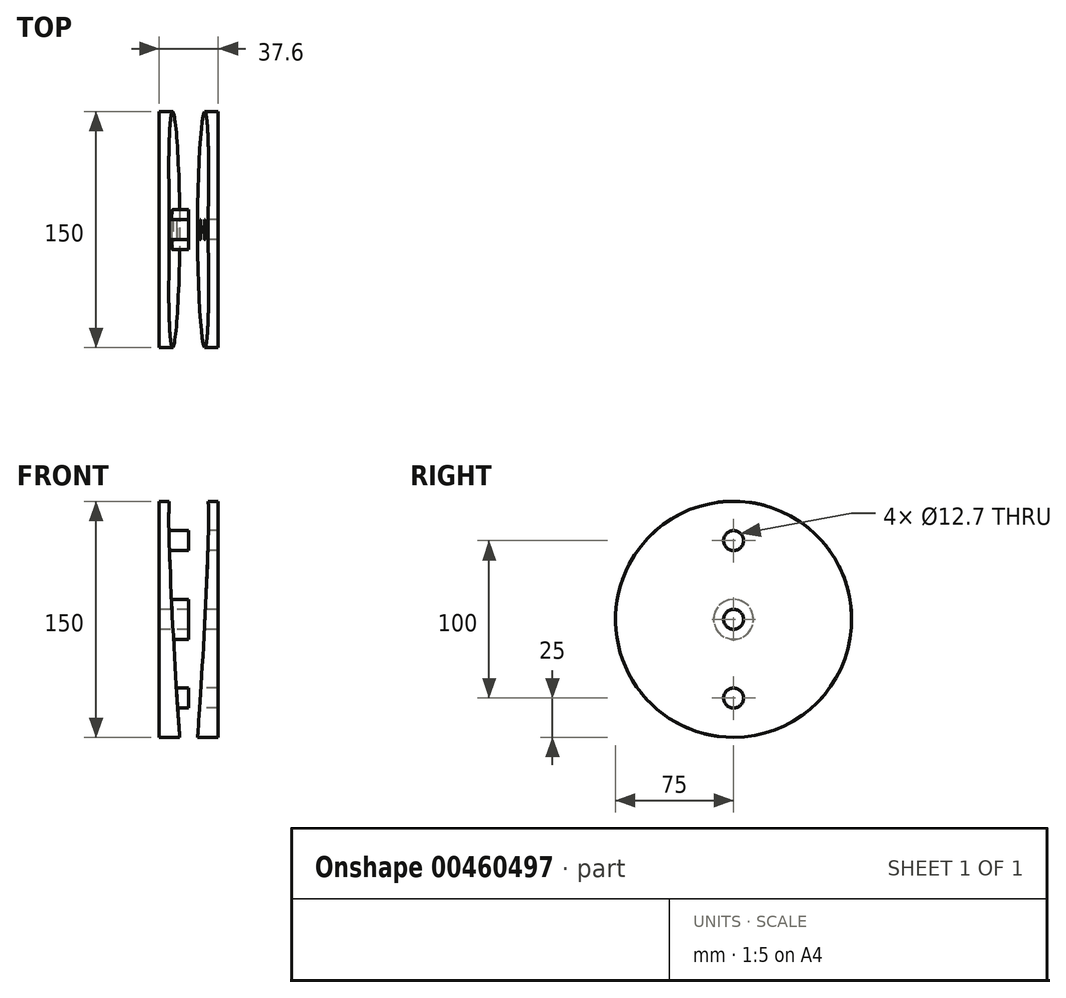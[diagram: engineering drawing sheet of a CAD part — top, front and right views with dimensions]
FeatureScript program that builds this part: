
annotation { "Feature Type Name" : "Feature", "Feature Type Description" : "" }
export const myFeature = defineFeature(function(context is Context, id is Id, definition is map)
    precondition{}
    {
        {
            var Q0;
            Q0=qCreatedBy(makeId("Front.planeOp"),FACE);
            var sketch = newSketch(context, id + "F0", { "sketchPlane" : qUnion([Q0])});
            skLineSegment(sketch, "E0", {"start": v(-26, 84.74) * mm, "end": v(-24.5, 84.74) * mm});
            skArc(sketch, "E1", {"start": v(-26.25, 85) * mm, "mid": v(-26.17, 84.82) * mm, "end": v(-26, 84.74) * mm});
            skFitSpline(sketch, "E2", {"points": [v(-26.25, 85) * mm, v(-26.24, 88.67) * mm, v(-26.08, 98.58) * mm, v(-25.1, 113) * mm, v(-22.87, 125.21) * mm, v(-20.9, 130.42) * mm, v(-19.33, 133.17) * mm, v(-17.9, 134.65) * mm, v(-16.79, 135) * mm, v(-16.24, 135) * mm]});
            skFitSpline(sketch, "E3", {"points": [v(-16.24, 135) * mm, v(-15.7, 135) * mm, v(-14.58, 134.65) * mm, v(-13.16, 133.17) * mm, v(-11.58, 130.42) * mm, v(-9.61, 125.21) * mm, v(-7.38, 113) * mm, v(-6.4, 98.58) * mm, v(-6.24, 88.67) * mm, v(-6.24, 85) * mm]});
            skArc(sketch, "E4", {"start": v(-6.49, 84.74) * mm, "mid": v(-6.3, 84.82) * mm, "end": v(-6.24, 85) * mm});
            skLineSegment(sketch, "E5", {"start": v(-7.99, 84.74) * mm, "end": v(-6.49, 84.74) * mm});
            skArc(sketch, "E6", {"start": v(-7.99, 84.74) * mm, "mid": v(-8.16, 84.67) * mm, "end": v(-8.24, 84.5) * mm});
            skLineSegment(sketch, "E7", {"start": v(-8.24, 84.5) * mm, "end": v(-8.24, 75) * mm});
            skArc(sketch, "E8", {"start": v(-10.24, 88.79) * mm, "mid": v(-10.27, 88.98) * mm, "end": v(-10.38, 89.14) * mm});
            skLineSegment(sketch, "E9", {"start": v(-11.41, 90.17) * mm, "end": v(-10.38, 89.14) * mm});
            skArc(sketch, "E10", {"start": v(-11.44, 90.85) * mm, "mid": v(-11.56, 90.5) * mm, "end": v(-11.41, 90.17) * mm});
            skArc(sketch, "E11", {"start": v(-11.44, 90.85) * mm, "mid": v(-9.9, 95) * mm, "end": v(-11.44, 99.15) * mm});
            skArc(sketch, "E12", {"start": v(-11.41, 99.83) * mm, "mid": v(-11.56, 99.5) * mm, "end": v(-11.44, 99.15) * mm});
            skLineSegment(sketch, "E13", {"start": v(-11.41, 99.83) * mm, "end": v(-9.68, 101.56) * mm});
            skArc(sketch, "E14", {"start": v(-9.68, 101.56) * mm, "mid": v(-9, 102.63) * mm, "end": v(-8.81, 103.89) * mm});
            skFitSpline(sketch, "E15", {"points": [v(-8.81, 103.89) * mm, v(-8.97, 106.15) * mm, v(-9.72, 114.71) * mm, v(-11.32, 123.38) * mm, v(-12.63, 127.4) * mm, v(-12.98, 128.32) * mm]});
            skArc(sketch, "E16", {"start": v(-12.98, 128.32) * mm, "mid": v(-13.34, 128.63) * mm, "end": v(-13.8, 128.5) * mm});
            skArc(sketch, "E17", {"start": v(-14.5, 127.97) * mm, "mid": v(-14.13, 128.21) * mm, "end": v(-13.8, 128.5) * mm});
            skArc(sketch, "E18", {"start": v(-15.24, 128.4) * mm, "mid": v(-15, 127.97) * mm, "end": v(-14.5, 127.97) * mm});
            skLineSegment(sketch, "E19", {"start": v(-15.24, 129) * mm, "end": v(-15.24, 128.4) * mm});
            skArc(sketch, "E20", {"start": v(-15.04, 129.4) * mm, "mid": v(-15.19, 129.22) * mm, "end": v(-15.24, 129) * mm});
            skArc(sketch, "E21", {"start": v(-15.04, 129.4) * mm, "mid": v(-16.24, 133) * mm, "end": v(-17.44, 129.4) * mm});
            skArc(sketch, "E22", {"start": v(-17.24, 129) * mm, "mid": v(-17.3, 129.22) * mm, "end": v(-17.44, 129.4) * mm});
            skLineSegment(sketch, "E23", {"start": v(-17.24, 128.4) * mm, "end": v(-17.24, 129) * mm});
            skArc(sketch, "E24", {"start": v(-18, 127.97) * mm, "mid": v(-17.5, 127.97) * mm, "end": v(-17.24, 128.4) * mm});
            skArc(sketch, "E25", {"start": v(-18.69, 128.5) * mm, "mid": v(-18.36, 128.21) * mm, "end": v(-18, 127.97) * mm});
            skArc(sketch, "E26", {"start": v(-18.69, 128.5) * mm, "mid": v(-19.15, 128.63) * mm, "end": v(-19.5, 128.32) * mm});
            skFitSpline(sketch, "E27", {"points": [v(-19.5, 128.32) * mm, v(-19.86, 127.4) * mm, v(-21.16, 123.38) * mm, v(-22.76, 114.71) * mm, v(-23.52, 106.15) * mm, v(-23.67, 103.89) * mm]});
            skArc(sketch, "E28", {"start": v(-23.67, 103.89) * mm, "mid": v(-23.49, 102.63) * mm, "end": v(-22.8, 101.56) * mm});
            skLineSegment(sketch, "E29", {"start": v(-22.8, 101.56) * mm, "end": v(-21.07, 99.83) * mm});
            skArc(sketch, "E30", {"start": v(-21.05, 99.15) * mm, "mid": v(-20.93, 99.5) * mm, "end": v(-21.07, 99.83) * mm});
            skArc(sketch, "E31", {"start": v(-21.05, 99.15) * mm, "mid": v(-22.6, 95) * mm, "end": v(-21.05, 90.85) * mm});
            skArc(sketch, "E32", {"start": v(-21.07, 90.17) * mm, "mid": v(-20.93, 90.5) * mm, "end": v(-21.05, 90.85) * mm});
            skLineSegment(sketch, "E33", {"start": v(-22.1, 89.14) * mm, "end": v(-21.07, 90.17) * mm});
            skArc(sketch, "E34", {"start": v(-22.1, 89.14) * mm, "mid": v(-22.2, 88.98) * mm, "end": v(-22.25, 88.79) * mm});
            skLineSegment(sketch, "E35", {"start": v(-24.25, 75) * mm, "end": v(-24.25, 84.5) * mm});
            skArc(sketch, "E36", {"start": v(-24.25, 84.5) * mm, "mid": v(-24.32, 84.67) * mm, "end": v(-24.5, 84.74) * mm});
            skLineSegment(sketch, "E37", {"start": v(-8.24, 75) * mm, "end": v(-10.24, 75) * mm});
            skLineSegment(sketch, "E38", {"start": v(-22.25, 88.79) * mm, "end": v(-22.25, 75) * mm});
            skLineSegment(sketch, "E39", {"start": v(-22.25, 75) * mm, "end": v(-24.25, 75) * mm});
            skLineSegment(sketch, "E40", {"start": v(-10.24, 75) * mm, "end": v(-10.24, 88.79) * mm});
            skArc(sketch, "E41", {"start": v(1.9, 35) * mm, "mid": v(5.19, -30.83) * mm, "end": v(9.73, -96.58) * mm});
            skFitSpline(sketch, "E42", {"points": [v(1.9, 35) * mm, v(1.67, 41.44) * mm, v(1.23, 54.34) * mm, v(1.24, 72.62) * mm, v(1.85, 89.82) * mm, v(2.95, 103.2) * mm, v(4.43, 113.85) * mm, v(5.71, 120.45) * mm, v(7.11, 125.63) * mm, v(8.23, 128.8) * mm, v(9.37, 131.23) * mm, v(10.3, 132.77) * mm, v(11.33, 133.95) * mm, v(12.42, 134.8) * mm, v(13.31, 134.93) * mm, v(13.76, 135) * mm]});
            skFitSpline(sketch, "E43", {"points": [v(25.63, 35) * mm, v(25.85, 41.44) * mm, v(26.29, 54.34) * mm, v(26.28, 72.62) * mm, v(25.66, 89.82) * mm, v(24.57, 103.2) * mm, v(23.09, 113.85) * mm, v(21.8, 120.45) * mm, v(20.4, 125.63) * mm, v(19.3, 128.8) * mm, v(18.15, 131.23) * mm, v(17.2, 132.77) * mm, v(16.18, 133.95) * mm, v(15.1, 134.8) * mm, v(14.2, 134.93) * mm, v(13.76, 135) * mm]});
            skArc(sketch, "E44", {"start": v(17.78, -96.58) * mm, "mid": v(22.33, -30.83) * mm, "end": v(25.63, 35) * mm});
            skLineSegment(sketch, "E45", {"start": v(14.84, -134) * mm, "end": v(17.78, -96.58) * mm});
            skLineSegment(sketch, "E46", {"start": v(12.68, -134) * mm, "end": v(9.73, -96.58) * mm});
            skArc(sketch, "E47", {"start": v(11.9, 127.93) * mm, "mid": v(12.51, 128.6) * mm, "end": v(12.32, 129.5) * mm});
            skArc(sketch, "E48", {"start": v(11.9, 127.93) * mm, "mid": v(11.17, 127.47) * mm, "end": v(10.7, 126.74) * mm});
            skFitSpline(sketch, "E49", {"points": [v(6.52, 106.91) * mm, v(6.59, 107.43) * mm, v(7.07, 111.18) * mm, v(8.03, 116.97) * mm, v(9.45, 123.07) * mm, v(10.41, 125.9) * mm, v(10.7, 126.74) * mm]});
            skArc(sketch, "E50", {"start": v(6.52, 106.91) * mm, "mid": v(6.84, 105.55) * mm, "end": v(7.98, 104.73) * mm});
            skArc(sketch, "E51", {"start": v(9.43, 103.98) * mm, "mid": v(8.75, 104.44) * mm, "end": v(7.98, 104.73) * mm});
            skArc(sketch, "E52", {"start": v(8.16, 102.44) * mm, "mid": v(9.56, 102.57) * mm, "end": v(9.43, 103.98) * mm});
            skArc(sketch, "E53", {"start": v(8.16, 102.44) * mm, "mid": v(5.1, 101) * mm, "end": v(8.16, 99.56) * mm});
            skArc(sketch, "E54", {"start": v(9.43, 98.02) * mm, "mid": v(9.56, 99.43) * mm, "end": v(8.16, 99.56) * mm});
            skArc(sketch, "E55", {"start": v(7.22, 97.14) * mm, "mid": v(8.4, 97.4) * mm, "end": v(9.43, 98.02) * mm});
            skArc(sketch, "E56", {"start": v(7.22, 97.14) * mm, "mid": v(5.94, 96.56) * mm, "end": v(5.36, 95.3) * mm});
            skLineSegment(sketch, "E57", {"start": v(5.28, 94.32) * mm, "end": v(5.36, 95.3) * mm});
            skArc(sketch, "E58", {"start": v(5.28, 94.32) * mm, "mid": v(4.02, 90.49) * mm, "end": v(4.8, 86.54) * mm});
            skLineSegment(sketch, "E59", {"start": v(4.72, 84.84) * mm, "end": v(4.8, 86.54) * mm});
            skArc(sketch, "E60", {"start": v(4.72, 84.84) * mm, "mid": v(3.54, 80.36) * mm, "end": v(4.4, 75.81) * mm});
            skLineSegment(sketch, "E61", {"start": v(4.4, 75.18) * mm, "end": v(4.4, 75.81) * mm});
            skArc(sketch, "E62", {"start": v(4.4, 75.18) * mm, "mid": v(3.3, 70.2) * mm, "end": v(4.27, 65.18) * mm});
            skLineSegment(sketch, "E63", {"start": v(4.31, 56.5) * mm, "end": v(4.27, 65.18) * mm});
            skArc(sketch, "E64", {"start": v(4.31, 56.5) * mm, "mid": v(5.37, 53.13) * mm, "end": v(6.65, 56.42) * mm});
            skArc(sketch, "E65", {"start": v(7.96, 57.93) * mm, "mid": v(6.55, 57.83) * mm, "end": v(6.65, 56.42) * mm});
            skArc(sketch, "E66", {"start": v(6.1, 51.19) * mm, "mid": v(9.16, 53.97) * mm, "end": v(7.96, 57.93) * mm});
            skArc(sketch, "E67", {"start": v(6.1, 51.19) * mm, "mid": v(4.9, 50.49) * mm, "end": v(4.44, 49.17) * mm});
            skLineSegment(sketch, "E68", {"start": v(4.89, 35.12) * mm, "end": v(4.44, 49.17) * mm});
            skArc(sketch, "E69", {"start": v(4.89, 35.12) * mm, "mid": v(5.23, 26.93) * mm, "end": v(5.6, 18.75) * mm});
            skArc(sketch, "E70", {"start": v(5.6, 18.75) * mm, "mid": v(6.13, 17.47) * mm, "end": v(7.37, 16.85) * mm});
            skArc(sketch, "E71", {"start": v(9.43, 15.98) * mm, "mid": v(8.46, 16.57) * mm, "end": v(7.37, 16.85) * mm});
            skArc(sketch, "E72", {"start": v(8.15, 14.44) * mm, "mid": v(9.56, 14.57) * mm, "end": v(9.43, 15.98) * mm});
            skArc(sketch, "E73", {"start": v(8.15, 14.44) * mm, "mid": v(5.09, 13) * mm, "end": v(8.15, 11.56) * mm});
            skArc(sketch, "E74", {"start": v(9.43, 10.02) * mm, "mid": v(9.56, 11.43) * mm, "end": v(8.15, 11.56) * mm});
            skArc(sketch, "E75", {"start": v(7.73, 9.2) * mm, "mid": v(8.63, 9.5) * mm, "end": v(9.43, 10.02) * mm});
            skArc(sketch, "E76", {"start": v(7.73, 9.2) * mm, "mid": v(6.55, 8.48) * mm, "end": v(6.14, 7.15) * mm});
            skArc(sketch, "E77", {"start": v(6.14, 7.15) * mm, "mid": v(9.04, -44.62) * mm, "end": v(12.73, -96.34) * mm});
            skLineSegment(sketch, "E78", {"start": v(12.76, -96.8) * mm, "end": v(12.73, -96.34) * mm});
            skArc(sketch, "E79", {"start": v(12.76, -96.8) * mm, "mid": v(13.76, -97.72) * mm, "end": v(14.76, -96.8) * mm});
            skLineSegment(sketch, "E80", {"start": v(14.76, -96.8) * mm, "end": v(14.8, -96.34) * mm});
            skArc(sketch, "E81", {"start": v(14.8, -96.34) * mm, "mid": v(18.47, -44.62) * mm, "end": v(21.38, 7.15) * mm});
            skArc(sketch, "E82", {"start": v(21.38, 7.15) * mm, "mid": v(20.96, 8.48) * mm, "end": v(19.78, 9.2) * mm});
            skArc(sketch, "E83", {"start": v(18.1, 10.02) * mm, "mid": v(18.89, 9.5) * mm, "end": v(19.78, 9.2) * mm});
            skArc(sketch, "E84", {"start": v(19.37, 11.56) * mm, "mid": v(17.96, 11.43) * mm, "end": v(18.1, 10.02) * mm});
            skArc(sketch, "E85", {"start": v(19.37, 11.56) * mm, "mid": v(22.43, 13) * mm, "end": v(19.37, 14.44) * mm});
            skArc(sketch, "E86", {"start": v(20.14, 16.85) * mm, "mid": v(19.05, 16.57) * mm, "end": v(18.1, 15.98) * mm});
            skArc(sketch, "E87", {"start": v(20.14, 16.85) * mm, "mid": v(21.39, 17.47) * mm, "end": v(21.93, 18.75) * mm});
            skArc(sketch, "E88", {"start": v(21.93, 18.75) * mm, "mid": v(22.29, 26.93) * mm, "end": v(22.63, 35.12) * mm});
            skLineSegment(sketch, "E89", {"start": v(22.63, 35.12) * mm, "end": v(23.08, 49.17) * mm});
            skArc(sketch, "E90", {"start": v(23.08, 49.17) * mm, "mid": v(22.62, 50.49) * mm, "end": v(21.42, 51.19) * mm});
            skArc(sketch, "E91", {"start": v(19.56, 57.93) * mm, "mid": v(18.35, 53.97) * mm, "end": v(21.42, 51.19) * mm});
            skArc(sketch, "E92", {"start": v(20.87, 56.42) * mm, "mid": v(20.97, 57.83) * mm, "end": v(19.56, 57.93) * mm});
            skArc(sketch, "E93", {"start": v(20.87, 56.42) * mm, "mid": v(22.15, 53.13) * mm, "end": v(23.2, 56.5) * mm});
            skLineSegment(sketch, "E94", {"start": v(23.2, 56.5) * mm, "end": v(23.25, 65.18) * mm});
            skArc(sketch, "E95", {"start": v(23.25, 65.18) * mm, "mid": v(24.2, 70.2) * mm, "end": v(23.12, 75.18) * mm});
            skArc(sketch, "E96", {"start": v(23.1, 75.81) * mm, "mid": v(23.98, 80.36) * mm, "end": v(22.8, 84.84) * mm});
            skLineSegment(sketch, "E97", {"start": v(22.8, 84.84) * mm, "end": v(22.71, 86.54) * mm});
            skArc(sketch, "E98", {"start": v(22.71, 86.54) * mm, "mid": v(23.5, 90.49) * mm, "end": v(22.23, 94.32) * mm});
            skLineSegment(sketch, "E99", {"start": v(22.23, 94.32) * mm, "end": v(22.16, 95.3) * mm});
            skArc(sketch, "E100", {"start": v(22.16, 95.3) * mm, "mid": v(21.57, 96.56) * mm, "end": v(20.3, 97.14) * mm});
            skArc(sketch, "E101", {"start": v(18.09, 98.02) * mm, "mid": v(19.12, 97.4) * mm, "end": v(20.3, 97.14) * mm});
            skArc(sketch, "E102", {"start": v(19.36, 99.56) * mm, "mid": v(17.95, 99.43) * mm, "end": v(18.09, 98.02) * mm});
            skArc(sketch, "E103", {"start": v(19.36, 99.56) * mm, "mid": v(22.42, 101) * mm, "end": v(19.36, 102.44) * mm});
            skArc(sketch, "E104", {"start": v(18.09, 103.98) * mm, "mid": v(17.95, 102.57) * mm, "end": v(19.36, 102.44) * mm});
            skArc(sketch, "E105", {"start": v(19.54, 104.73) * mm, "mid": v(18.77, 104.44) * mm, "end": v(18.09, 103.98) * mm});
            skArc(sketch, "E106", {"start": v(19.54, 104.73) * mm, "mid": v(20.67, 105.55) * mm, "end": v(21, 106.91) * mm});
            skFitSpline(sketch, "E107", {"points": [v(21, 106.91) * mm, v(20.93, 107.43) * mm, v(20.44, 111.18) * mm, v(19.49, 116.97) * mm, v(18.07, 123.07) * mm, v(17.1, 125.9) * mm, v(16.81, 126.74) * mm]});
            skArc(sketch, "E108", {"start": v(16.81, 126.74) * mm, "mid": v(16.35, 127.47) * mm, "end": v(15.62, 127.93) * mm});
            skArc(sketch, "E109", {"start": v(15.2, 129.5) * mm, "mid": v(15, 128.6) * mm, "end": v(15.62, 127.93) * mm});
            skArc(sketch, "E110", {"start": v(15.2, 129.5) * mm, "mid": v(13.76, 132.57) * mm, "end": v(12.32, 129.5) * mm});
            skArc(sketch, "E111", {"start": v(18.1, 15.98) * mm, "mid": v(17.96, 14.57) * mm, "end": v(19.37, 14.44) * mm});
            skArc(sketch, "E112", {"start": v(12.68, -134) * mm, "mid": v(13.76, -135) * mm, "end": v(14.84, -134) * mm});
            skLineSegment(sketch, "E113", {"start": v(23.12, 75.18) * mm, "end": v(23.1, 75.81) * mm});
            skSolve(sketch);
        }
        {
            var Q0;
            Q0=makeQuery(id+"F0.imprint","IMPRINT",FACE,{"disambiguationData":[TD([[makeQuery(id+"F0.imprint","IMPRINT",EDGE,{"derivedFrom":sQuery(id+"F0.wireOp",EDGE,"E41")}),1.0]])]});
            extrude(context, id + "F1", {"entities" : qUnion([Q0]), "offsetDistance" : 25 * mm, "depth" : 1028 * mm});
        }
        {
            var Q0;
            Q0=qCreatedBy(makeId("Right.planeOp"),FACE);
            var sketch = newSketch(context, id + "F2", { "sketchPlane" : qUnion([Q0])});
            skCircle(sketch, "E114", {"center": v(-135, 0) * mm, "radius": 135 * mm, "construction": true});
            skLineSegment(sketch, "E115", {"start": v(-135, 135) * mm, "end": v(-18.09, 67.5) * mm});
            skLineSegment(sketch, "E116", {"start": v(-18.09, 67.5) * mm, "end": v(-18.09, -67.5) * mm});
            skLineSegment(sketch, "E117", {"start": v(-18.09, -67.5) * mm, "end": v(-135, -135) * mm});
            skLineSegment(sketch, "E118", {"start": v(-135, -135) * mm, "end": v(-135, 135) * mm, "construction": true});
            skLineSegment(sketch, "E119", {"start": v(-135, 135) * mm, "end": v(0, 203.42) * mm});
            skLineSegment(sketch, "E120", {"start": v(0, 203.42) * mm, "end": v(0, -205.94) * mm});
            skLineSegment(sketch, "E121", {"start": v(0, -205.94) * mm, "end": v(-135, -135) * mm});
            skSolve(sketch);
        }
        {
            var Q0;
            Q0 = qSketchRegion(id + "F2", true);
            extrude(context, id + "F3", {"entities" : qUnion([Q0]), "operationType" : NewBodyOperationType.REMOVE, "endBound" : BoundingType.THROUGH_ALL, "depth" : 25 * mm, "offsetDistance" : 25 * mm});
        }
        {
            var Q0;
            Q0=qCreatedBy(makeId("Front.planeOp"),FACE);
            var sketch = newSketch(context, id + "F4", { "sketchPlane" : qUnion([Q0])});
            skLineSegment(sketch, "E122.bottom", {"start": v(32.56, 135) * mm, "end": v(-5.04, 135) * mm});
            skLineSegment(sketch, "E122.top", {"start": v(32.56, -135) * mm, "end": v(-5.04, -135) * mm});
            skLineSegment(sketch, "E122.left", {"start": v(32.56, 135) * mm, "end": v(32.56, -135) * mm});
            skLineSegment(sketch, "E122.right", {"start": v(-5.04, 135) * mm, "end": v(-5.04, -135) * mm});
            skSolve(sketch);
        }
        {
            var Q0;
            Q0=qSketchRegion(id+"F4",true);
            extrude(context, id + "F5", {"entities" : qUnion([Q0]), "depth" : 280 * mm, "offsetDistance" : 25 * mm});
        }
        {
            var Q0;
            Q0=makeQuery(id+"F5.opExtrude","SWEPT_FACE",FACE,{"disambiguationData":[OSD([sQuery(id+"F4.wireOp",EDGE,"E122.right")])]});
            var sketch = newSketch(context, id + "F6", { "sketchPlane" : qUnion([Q0])});
            skCircle(sketch, "E123", {"center": v(135, 0) * mm, "radius": 75 * mm});
            skLineSegment(sketch, "E124", {"start": v(0, 0) * mm, "end": v(135, 0) * mm, "construction": true});
            skSolve(sketch);
        }
        {
            var Q0;
            Q0 = qSketchRegion(id + "F6", true);
            extrude(context, id + "F7", {"entities" : qUnion([Q0]), "operationType" : NewBodyOperationType.INTERSECT, "endBound" : BoundingType.THROUGH_ALL, "oppositeDirection" : true, "depth" : 25 * mm, "offsetDistance" : 25 * mm});
        }
        {
            var Q0;
            Q0=qCreatedBy(makeId("Front.planeOp"),FACE);
            var sketch = newSketch(context, id + "F8", { "sketchPlane" : qUnion([Q0])});
            skFitSpline(sketch, "E125.0", {"points": [v(25.63, 35) * mm, v(25.85, 41.44) * mm, v(26.29, 54.34) * mm, v(26.28, 72.62) * mm, v(25.66, 89.82) * mm, v(24.57, 103.2) * mm, v(23.09, 113.85) * mm, v(21.8, 120.45) * mm, v(20.4, 125.63) * mm, v(19.3, 128.8) * mm, v(18.15, 131.23) * mm, v(17.2, 132.77) * mm, v(16.18, 133.95) * mm, v(15.1, 134.8) * mm, v(14.2, 134.93) * mm, v(13.76, 135) * mm]});
            skFitSpline(sketch, "E126.0", {"points": [v(1.9, 35) * mm, v(1.67, 41.44) * mm, v(1.23, 54.34) * mm, v(1.24, 72.62) * mm, v(1.85, 89.82) * mm, v(2.95, 103.2) * mm, v(4.43, 113.85) * mm, v(5.71, 120.45) * mm, v(7.11, 125.63) * mm, v(8.23, 128.8) * mm, v(9.37, 131.23) * mm, v(10.3, 132.77) * mm, v(11.33, 133.95) * mm, v(12.42, 134.8) * mm, v(13.31, 134.93) * mm, v(13.76, 135) * mm]});
            skArc(sketch, "E127.0", {"start": v(1.9, 35) * mm, "mid": v(5.19, -30.83) * mm, "end": v(9.73, -96.58) * mm});
            skArc(sketch, "E128.0", {"start": v(17.78, -96.58) * mm, "mid": v(22.33, -30.83) * mm, "end": v(25.63, 35) * mm});
            skLineSegment(sketch, "E129.0", {"start": v(14.84, -134) * mm, "end": v(17.78, -96.58) * mm});
            skLineSegment(sketch, "E130.0", {"start": v(12.68, -134) * mm, "end": v(9.73, -96.58) * mm});
            skArc(sketch, "E131.0", {"start": v(12.68, -134) * mm, "mid": v(13.76, -135) * mm, "end": v(14.84, -134) * mm});
            skSolve(sketch);
        }
        {
            var Q0;
            Q0 = qSketchRegion(id + "F8", true);
            extrude(context, id + "F9", {"entities" : qUnion([Q0]), "operationType" : NewBodyOperationType.REMOVE, "endBound" : BoundingType.THROUGH_ALL, "depth" : 25 * mm, "offsetDistance" : 25 * mm});
        }
        {
            var Q0;
            Q0=makeQuery(id+"F5.opExtrude","SWEPT_FACE",FACE,{"disambiguationData":[OSD([sQuery(id+"F4.wireOp",EDGE,"E122.right")])]});
            var sketch = newSketch(context, id + "F10", { "sketchPlane" : qUnion([Q0])});
            skCircle(sketch, "E132", {"center": v(135, 0) * mm, "radius": 6.35 * mm});
            skCircle(sketch, "E133", {"center": v(135, 50) * mm, "radius": 6.35 * mm});
            skLineSegment(sketch, "E134", {"start": v(135, 0) * mm, "end": v(180.8, 0) * mm, "construction": true});
            skCircle(sketch, "E135.MirrorC", {"center": v(135, -50) * mm, "radius": 6.35 * mm});
            skSolve(sketch);
        }
        {
            var Q0;
            Q0 = qSketchRegion(id + "F10", true);
            extrude(context, id + "F11", {"entities" : qUnion([Q0]), "operationType" : NewBodyOperationType.REMOVE, "endBound" : BoundingType.THROUGH_ALL, "oppositeDirection" : true, "depth" : 25 * mm, "offsetDistance" : 25 * mm});
        }
        {
            var Q0;
            Q0=qCreatedBy(makeId("Right.planeOp"),FACE);
            var sketch = newSketch(context, id + "F12", { "sketchPlane" : qUnion([Q0])});
            skLineSegment(sketch, "E136.bottom", {"start": v(-18.09, 100.47) * mm, "end": v(-43.09, 100.47) * mm});
            skLineSegment(sketch, "E136.top", {"start": v(-18.09, -149.67) * mm, "end": v(-43.09, -149.67) * mm});
            skLineSegment(sketch, "E136.left", {"start": v(-18.09, 100.47) * mm, "end": v(-18.09, -149.67) * mm});
            skLineSegment(sketch, "E136.right", {"start": v(-43.09, 100.47) * mm, "end": v(-43.09, -149.67) * mm});
            skSolve(sketch);
        }
        {
            var Q0;
            Q0 = qSketchRegion(id + "F12", true);
            extrude(context, id + "F13", {"entities" : qUnion([Q0]), "operationType" : NewBodyOperationType.REMOVE, "endBound" : BoundingType.THROUGH_ALL, "depth" : 25 * mm, "offsetDistance" : 25 * mm});
        }
        {
            var Q0;
            Q0=makeQuery(id+"F5.opExtrude","SWEPT_FACE",FACE,{"disambiguationData":[OSD([sQuery(id+"F4.wireOp",EDGE,"E122.right")])]});
            var sketch = newSketch(context, id + "F14", { "sketchPlane" : qUnion([Q0])});
            skCircle(sketch, "E137.0", {"center": v(135, 50) * mm, "radius": 6.35 * mm});
            skCircle(sketch, "E138.0", {"center": v(135, 0) * mm, "radius": 6.35 * mm});
            skCircle(sketch, "E139.0", {"center": v(135, -50) * mm, "radius": 6.35 * mm});
            skCircle(sketch, "E140", {"center": v(135, 0) * mm, "radius": 12.7 * mm});
            skSolve(sketch);
        }
        {
            var Q0;
            Q0 = qSketchRegion(id + "F14", true);
            extrude(context, id + "F15", {"entities" : qUnion([Q0]), "operationType" : NewBodyOperationType.ADD, "oppositeDirection" : true, "depth" : 18.8 * mm, "offsetDistance" : 25 * mm});
        }
    });
